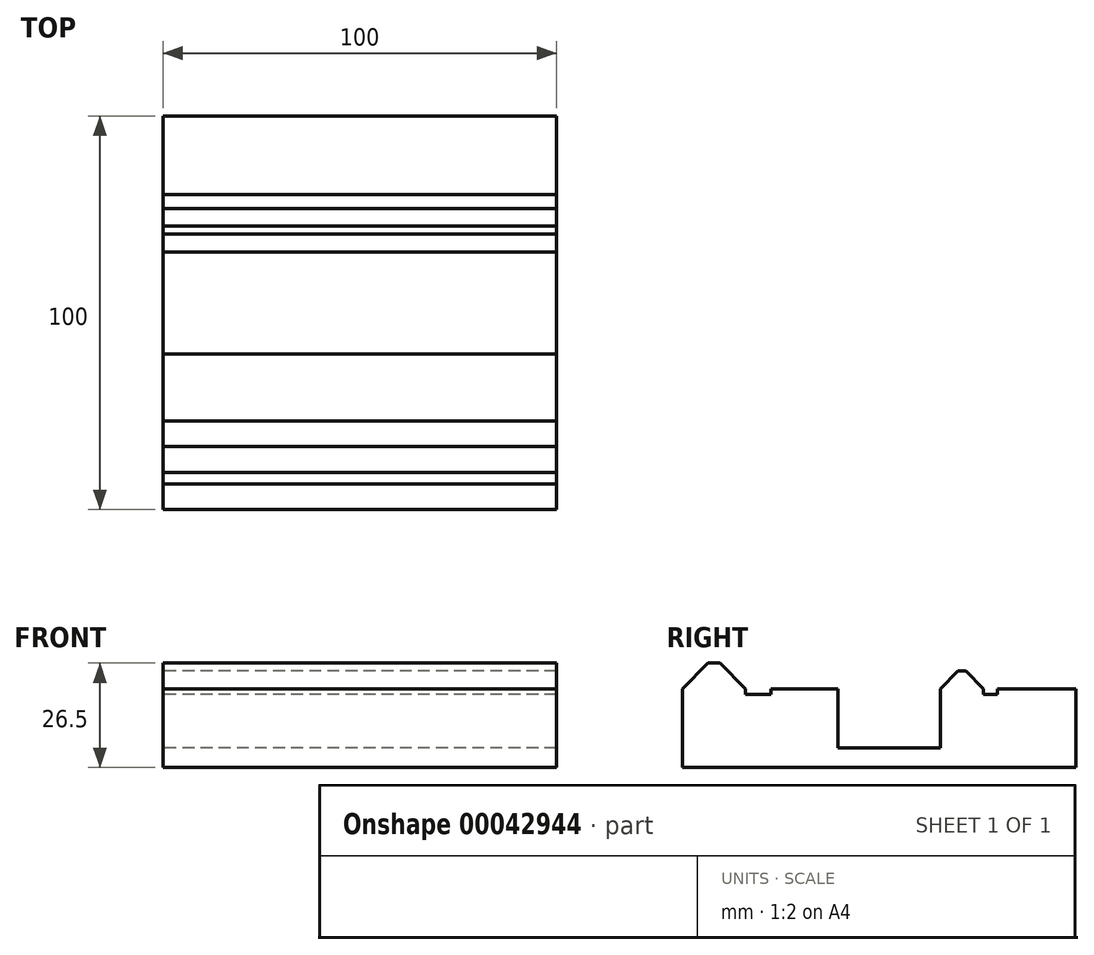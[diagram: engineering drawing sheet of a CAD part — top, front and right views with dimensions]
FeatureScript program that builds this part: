
annotation { "Feature Type Name" : "Feature", "Feature Type Description" : "" }
export const myFeature = defineFeature(function(context is Context, id is Id, definition is map)
    precondition{}
    {
        {
            var Q0;
            Q0=qCreatedBy(makeId("Right.planeOp"),FACE);
            var sketch = newSketch(context, id + "F0", { "sketchPlane" : qUnion([Q0])});
            skLineSegment(sketch, "E0", {"start": v(0, 0) * mm, "end": v(8, 8) * mm, "construction": true});
            skLineSegment(sketch, "E1", {"start": v(8, 8) * mm, "end": v(16, 0) * mm, "construction": true});
            skLineSegment(sketch, "E2", {"start": v(65.5, 0) * mm, "end": v(71, 5.5) * mm, "construction": true});
            skLineSegment(sketch, "E3", {"start": v(71, 5.5) * mm, "end": v(76.5, 0) * mm, "construction": true});
            skLineSegment(sketch, "E4", {"start": v(0, 0) * mm, "end": v(6.5, 6.5) * mm});
            skLineSegment(sketch, "E5", {"start": v(6.5, 6.5) * mm, "end": v(9.5, 6.5) * mm});
            skLineSegment(sketch, "E6", {"start": v(9.5, 6.5) * mm, "end": v(16, 0) * mm});
            skLineSegment(sketch, "E7", {"start": v(65.5, 0) * mm, "end": v(70, 4.5) * mm});
            skLineSegment(sketch, "E8", {"start": v(70, 4.5) * mm, "end": v(72, 4.5) * mm});
            skLineSegment(sketch, "E9", {"start": v(72, 4.5) * mm, "end": v(76.5, 0) * mm});
            skLineSegment(sketch, "E10", {"start": v(16, 0) * mm, "end": v(16, -1.5) * mm});
            skLineSegment(sketch, "E11", {"start": v(16, -1.5) * mm, "end": v(22.5, -1.5) * mm});
            skLineSegment(sketch, "E12", {"start": v(22.5, -1.5) * mm, "end": v(22.5, 0) * mm});
            skLineSegment(sketch, "E13", {"start": v(22.5, 0) * mm, "end": v(39.5, 0) * mm});
            skLineSegment(sketch, "E14", {"start": v(39.5, 0) * mm, "end": v(39.5, -15) * mm});
            skLineSegment(sketch, "E15", {"start": v(100, -20) * mm, "end": v(0, -20) * mm});
            skLineSegment(sketch, "E16", {"start": v(0, -20) * mm, "end": v(0, 0) * mm});
            skLineSegment(sketch, "E17", {"start": v(76.5, 0) * mm, "end": v(76.5, -1.5) * mm});
            skLineSegment(sketch, "E18", {"start": v(76.5, -1.5) * mm, "end": v(80, -1.5) * mm});
            skLineSegment(sketch, "E19", {"start": v(80, -1.5) * mm, "end": v(80, 0) * mm});
            skLineSegment(sketch, "E20", {"start": v(80, 0) * mm, "end": v(100, 0) * mm});
            skLineSegment(sketch, "E21", {"start": v(100, 0) * mm, "end": v(100, -20) * mm});
            skLineSegment(sketch, "E22", {"start": v(65.5, -15) * mm, "end": v(65.5, 0) * mm});
            skLineSegment(sketch, "E23", {"start": v(39.5, -15) * mm, "end": v(65.5, -15) * mm});
            skSolve(sketch);
        }
        {
            var Q0;
            Q0=makeQuery(id+"F0.imprint","IMPRINT",FACE,{"disambiguationData":[TD([[makeQuery(id+"F0.imprint","IMPRINT",EDGE,{"derivedFrom":sQuery(id+"F0.wireOp",EDGE,"E4")}),-1.0]])]});
            var Q1;
            Q1=makeQuery(id+"F0.imprint","IMPRINT",FACE,{"disambiguationData":[TD([[makeQuery(id+"F0.imprint","IMPRINT",EDGE,{"derivedFrom":sQuery(id+"F0.wireOp",EDGE,"E7")}),-1.0]])]});
            extrude(context, id + "F1", {"entities" : qUnion([Q0, Q1]), "depth" : 100 * mm});
        }
    });
